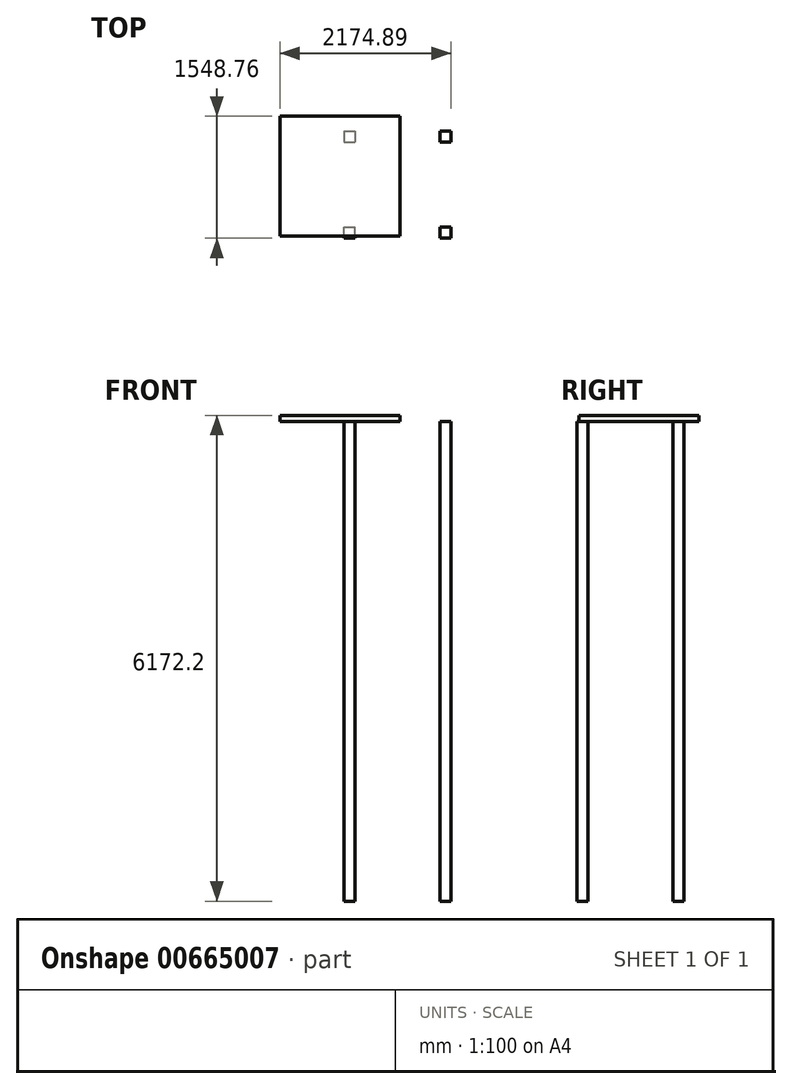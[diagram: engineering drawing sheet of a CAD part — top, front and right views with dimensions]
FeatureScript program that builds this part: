
annotation { "Feature Type Name" : "Feature", "Feature Type Description" : "" }
export const myFeature = defineFeature(function(context is Context, id is Id, definition is map)
    precondition{}
    {
        {
            var Q0;
            Q0=qCreatedBy(makeId("Top.planeOp"),FACE);
            var sketch = newSketch(context, id + "F0", { "sketchPlane" : qUnion([Q0])});
            skLineSegment(sketch, "E0.bottom", {"start": v(815.99, 22.6) * mm, "end": v(955.69, 22.6) * mm});
            skLineSegment(sketch, "E0.top", {"start": v(815.99, -117.1) * mm, "end": v(955.69, -117.1) * mm});
            skLineSegment(sketch, "E0.left", {"start": v(815.99, 22.6) * mm, "end": v(815.99, -117.1) * mm});
            skLineSegment(sketch, "E0.right", {"start": v(955.69, 22.6) * mm, "end": v(955.69, -117.1) * mm});
            skLineSegment(sketch, "E1", {"start": v(1495.44, 133.34) * mm, "end": v(1495.44, -2568.45) * mm, "construction": true});
            skLineSegment(sketch, "E2", {"start": v(885.84, 22.6) * mm, "end": v(885.84, -117.1) * mm, "construction": true});
            skLineSegment(sketch, "E3", {"start": v(815.99, -47.25) * mm, "end": v(955.69, -47.25) * mm, "construction": true});
            skLineSegment(sketch, "E4", {"start": v(-2.35, -656.85) * mm, "end": v(3622.6, -656.85) * mm, "construction": true});
            skLineSegment(sketch, "E5.MirrorCS", {"start": v(2035.19, 22.6) * mm, "end": v(2035.19, -117.1) * mm});
            skLineSegment(sketch, "E6.MirrorCS", {"start": v(2174.89, 22.6) * mm, "end": v(2035.19, 22.6) * mm});
            skLineSegment(sketch, "E7.MirrorCS", {"start": v(2174.89, 22.6) * mm, "end": v(2174.89, -117.1) * mm});
            skLineSegment(sketch, "E8.MirrorCS", {"start": v(2174.89, -117.1) * mm, "end": v(2035.19, -117.1) * mm});
            skLineSegment(sketch, "E9.MirrorCS", {"start": v(2105.04, 22.6) * mm, "end": v(2105.04, -117.1) * mm, "construction": true});
            skLineSegment(sketch, "E10.MirrorCS", {"start": v(2174.89, -47.25) * mm, "end": v(2035.19, -47.25) * mm, "construction": true});
            skLineSegment(sketch, "E11.MirrorCS", {"start": v(2174.89, -1336.3) * mm, "end": v(2174.89, -1196.6) * mm});
            skLineSegment(sketch, "E12.MirrorCS", {"start": v(815.99, -1336.3) * mm, "end": v(955.69, -1336.3) * mm});
            skLineSegment(sketch, "E13.MirrorCS", {"start": v(2174.89, -1336.3) * mm, "end": v(2035.19, -1336.3) * mm});
            skLineSegment(sketch, "E14.MirrorCS", {"start": v(2035.19, -1336.3) * mm, "end": v(2035.19, -1196.6) * mm});
            skLineSegment(sketch, "E15.MirrorCS", {"start": v(2174.89, -1196.6) * mm, "end": v(2035.19, -1196.6) * mm});
            skLineSegment(sketch, "E16.MirrorCS", {"start": v(815.99, -1196.6) * mm, "end": v(955.69, -1196.6) * mm});
            skLineSegment(sketch, "E17.MirrorCS", {"start": v(955.69, -1336.3) * mm, "end": v(955.69, -1196.6) * mm});
            skLineSegment(sketch, "E18.MirrorCS", {"start": v(815.99, -1336.3) * mm, "end": v(815.99, -1196.6) * mm});
            skLineSegment(sketch, "E19.MirrorCS", {"start": v(2105.04, -1336.3) * mm, "end": v(2105.04, -1196.6) * mm, "construction": true});
            skLineSegment(sketch, "E20.MirrorCS", {"start": v(2174.89, -1266.45) * mm, "end": v(2035.19, -1266.45) * mm, "construction": true});
            skLineSegment(sketch, "E21.MirrorCS", {"start": v(885.84, -1336.3) * mm, "end": v(885.84, -1196.6) * mm, "construction": true});
            skLineSegment(sketch, "E22.MirrorCS", {"start": v(815.99, -1266.45) * mm, "end": v(955.69, -1266.45) * mm, "construction": true});
            skSolve(sketch);
        }
        {
            var Q0;
            Q0 = qSketchRegion(id + "F0", true);
            extrude(context, id + "F1", {"entities" : qUnion([Q0]), "depth" : 6096 * mm, "offsetDistance" : 25.4 * mm});
        }
        {
            var Q0;
            Q0=makeQuery(id+"F1.opExtrude","CAP_FACE",FACE,{"disambiguationData":[OSD([sQuery(id+"F0.wireOp",EDGE,"E0.bottom"),sQuery(id+"F0.wireOp",EDGE,"E0.top"),sQuery(id+"F0.wireOp",EDGE,"E0.left"),sQuery(id+"F0.wireOp",EDGE,"E0.right")])],"isStart":false});
            var sketch = newSketch(context, id + "F2", { "sketchPlane" : qUnion([Q0])});
            skLineSegment(sketch, "E23.bottom", {"start": v(0, 212.46) * mm, "end": v(1524, 212.46) * mm});
            skLineSegment(sketch, "E23.top", {"start": v(0, -1311.54) * mm, "end": v(1524, -1311.54) * mm});
            skLineSegment(sketch, "E23.left", {"start": v(0, 212.46) * mm, "end": v(0, -1311.54) * mm});
            skLineSegment(sketch, "E23.right", {"start": v(1524, 212.46) * mm, "end": v(1524, -1311.54) * mm});
            skSolve(sketch);
        }
        {
            var Q0;
            Q0 = qSketchRegion(id + "F2", true);
            extrude(context, id + "F3", {"entities" : qUnion([Q0]), "operationType" : NewBodyOperationType.ADD, "depth" : 76.2 * mm, "offsetDistance" : 25.4 * mm});
        }
    });
